# Revit family: rba-bim-B1658 1639
name_source: partatom
category: Plumbing Fixtures
revit_build: Autodesk Revit 2018 (Build: 20170223_1515(x64)
units: mm (PartAtom-declared; Revit-internal decimal feet)

## family parameters
Always vertical = No
Cut with Voids When Loaded = No
Part Type = Normal
Room Calculation Point = No
Round Connector Dimension = Use Diameter
Shared = Yes
Work Plane-Based = Yes

## types (1)
- B1658 1639
    Accessible Compliant = AS1428.1-2009 Compliant
    Default Elevation = 1219.2 mm  [stored 4 ft]
    Description = Safety Glass Mirror with Stainless Steel Angle Frame to AS1428.1
    Frame Material = Stainless Steel - Bobrick - Satin
    Glass Material = Glass Mirror - Bobrick
    Manufacturer = Bobrick
    Mirror Background = Paint - Bobrick - Black
    Model = B1658 1639
    Modified Issue = 20220210.01

note: [stored X ft] marks values corroborated as IEEE doubles in the binary element streams (Revit-internal decimal feet)

## geometry (parser evidence)
native form markers: Blend x2, Sweep x3
no freeform markers — native parametric forms only
